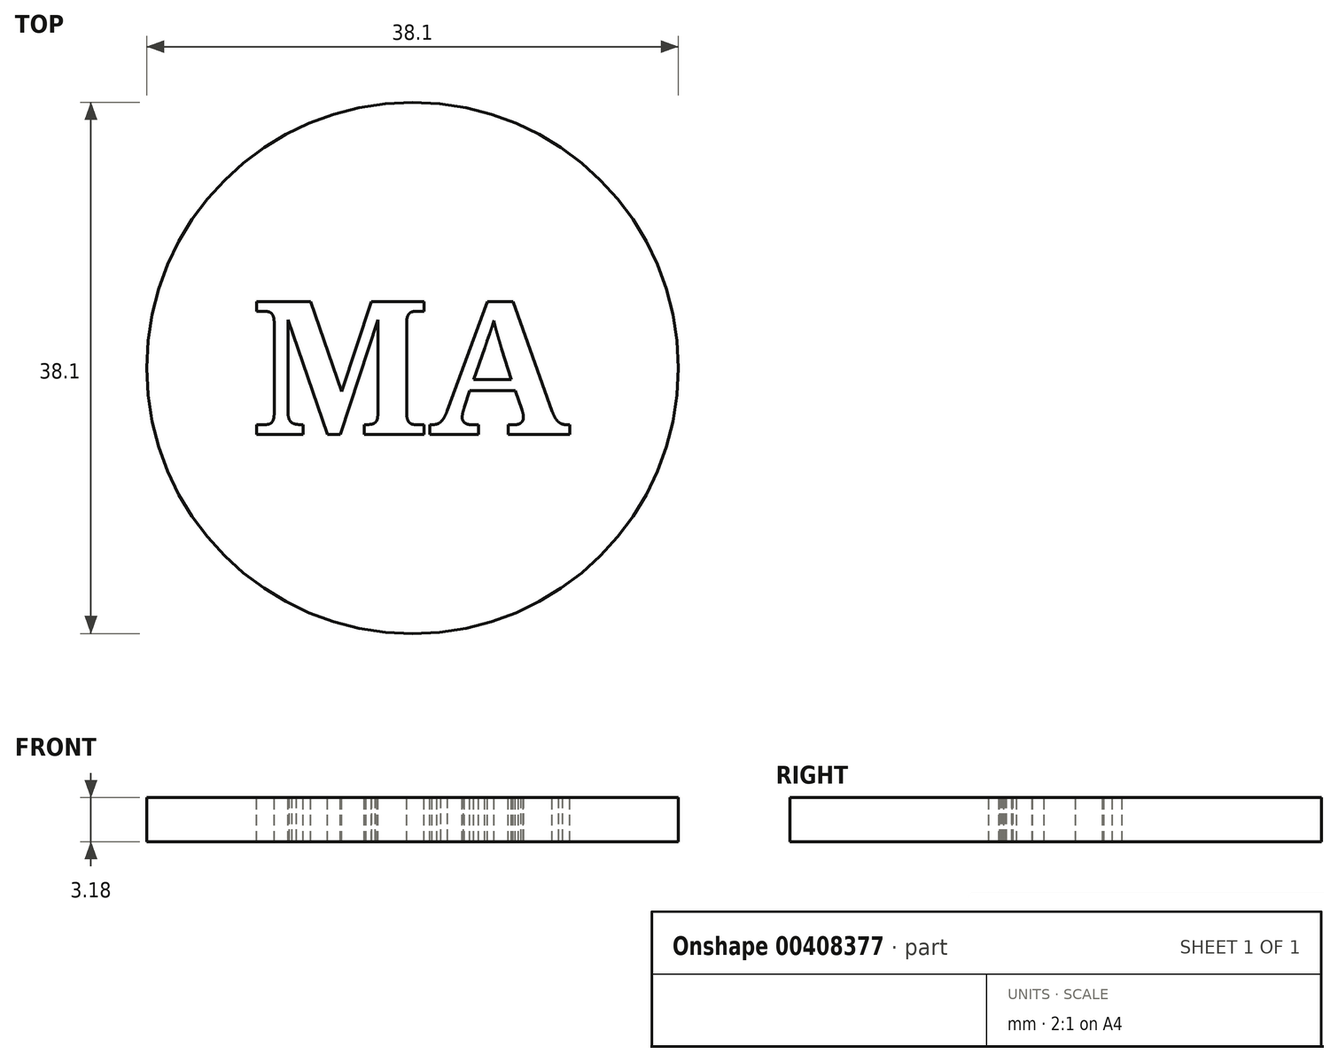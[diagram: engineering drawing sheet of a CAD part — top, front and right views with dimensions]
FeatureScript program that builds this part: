
annotation { "Feature Type Name" : "Feature", "Feature Type Description" : "" }
export const myFeature = defineFeature(function(context is Context, id is Id, definition is map)
    precondition{}
    {
        {
            var Q0;
            Q0=qCreatedBy(makeId("Front.planeOp"),FACE);
            var sketch = newSketch(context, id + "F0", { "sketchPlane" : qUnion([Q0])});
            skLineSegment(sketch, "E0.bottom", {"start": v(19.05, -1.68) * mm, "end": v(-19.05, -1.68) * mm});
            skLineSegment(sketch, "E0.top", {"start": v(19.05, 1.5) * mm, "end": v(-19.05, 1.5) * mm});
            skLineSegment(sketch, "E0.left", {"start": v(19.05, -1.68) * mm, "end": v(19.05, 1.5) * mm});
            skLineSegment(sketch, "E0.right", {"start": v(-19.05, -1.68) * mm, "end": v(-19.05, 1.5) * mm});
            skPoint(sketch, "E0.middle", {"position": v(0, -0.09) * mm});
            skLineSegment(sketch, "E1", {"start": v(0, 1.5) * mm, "end": v(0, -1.68) * mm});
            skSolve(sketch);
        }
        {
            var Q0;
            {var subQ0=sQuery(id+"F0.wireOp",EDGE,"E0.left");Q0=makeQuery(id+"F0.imprint","IMPRINT",FACE,{"disambiguationData":[TD([[makeQuery(id+"F0.imprint","IMPRINT",EDGE,{"derivedFrom":subQ0}),1.0]])]});}
            var Q1;
            Q1=sQuery(id+"F0.wireOp",EDGE,"E1");
            revolve(context, id + "F1", {"entities" : qUnion([Q0]), "axis" : qUnion([Q1]), "revolveType" : RevolveType.FULL});
        }
        {
            var Q0;
            Q0=qCreatedBy(makeId("Top.planeOp"),FACE);
            var sketch = newSketch(context, id + "F2", { "sketchPlane" : qUnion([Q0])});
            skText(sketch, "E2", { "text": "MA", "fontName": "NotoSerif-Bold.ttf"});
            const initialGuessF2  = {"E2": [-0.01154, -0.00478, 1, 0, 0.00963]};
            skSetInitialGuess(sketch, initialGuessF2);
            skSolve(sketch);
        }
        {
            var Q0;
            Q0 = qSketchRegion(id + "F2", true);
            extrude(context, id + "F3", {"entities" : qUnion([Q0]), "operationType" : NewBodyOperationType.REMOVE, "endBound" : BoundingType.SYMMETRIC, "oppositeDirection" : true, "depth" : 3.3 * mm});
        }
    });
